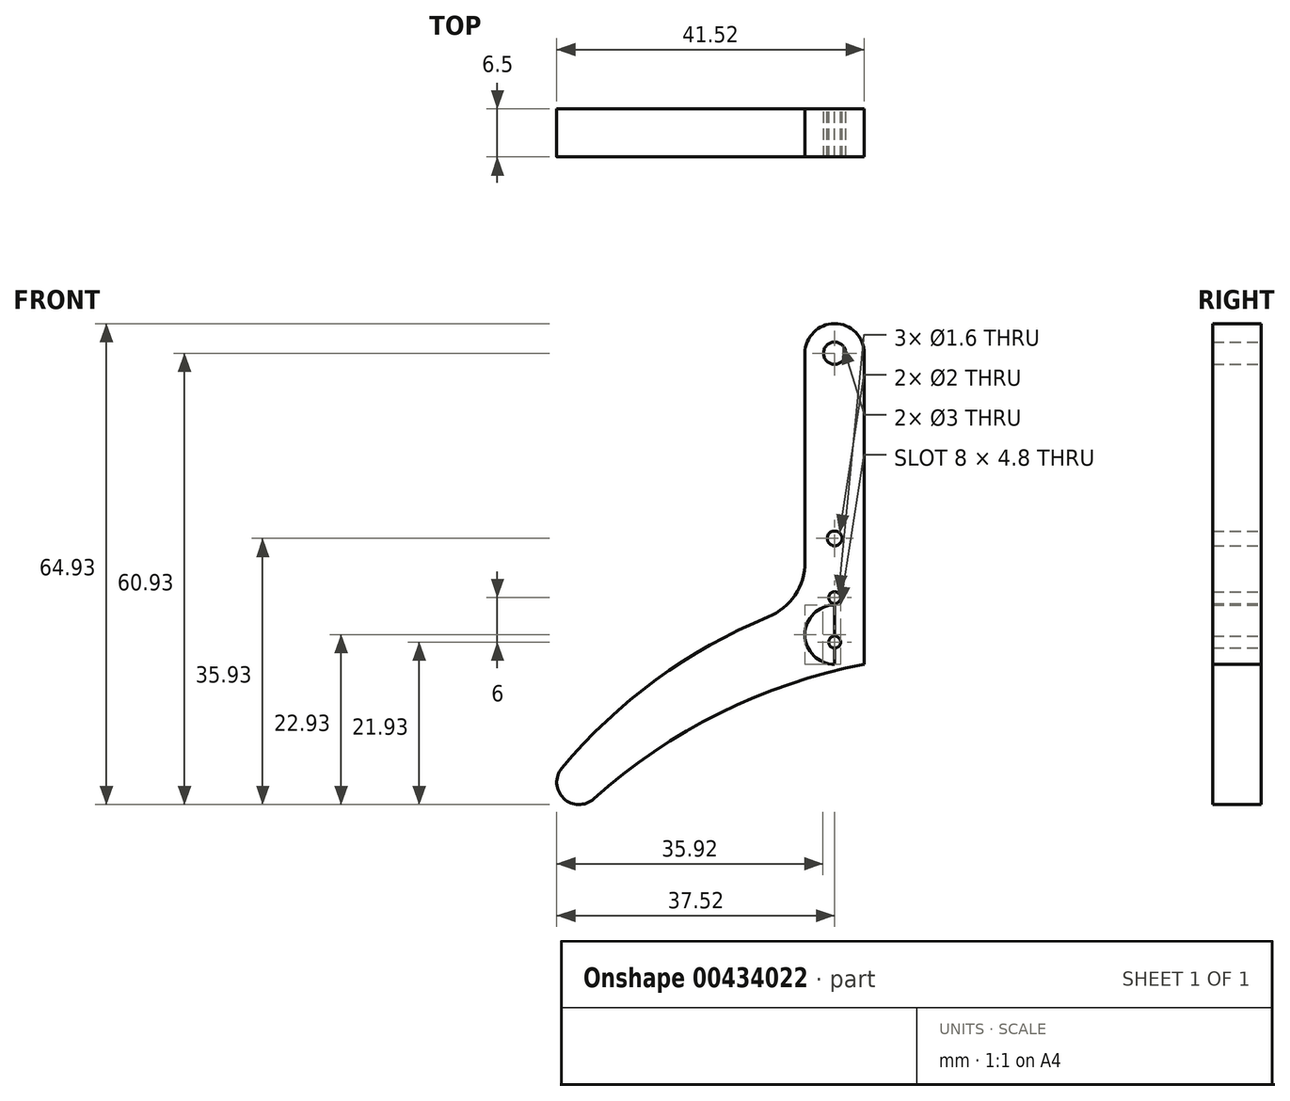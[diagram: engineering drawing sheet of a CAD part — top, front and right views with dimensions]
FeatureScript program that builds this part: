
annotation { "Feature Type Name" : "Feature", "Feature Type Description" : "" }
export const myFeature = defineFeature(function(context is Context, id is Id, definition is map)
    precondition{}
    {
        {
            var Q0;
            Q0=qCreatedBy(makeId("Front.planeOp"),FACE);
            var sketch = newSketch(context, id + "F0", { "sketchPlane" : qUnion([Q0])});
            skCircle(sketch, "E0", {"center": v(0, 38) * mm, "radius": 4 * mm});
            skCircle(sketch, "E1", {"center": v(0, 0) * mm, "radius": 4 * mm});
            skCircle(sketch, "E2", {"center": v(0, 38) * mm, "radius": 1.5 * mm});
            skCircle(sketch, "E3", {"center": v(-34.52, -19.93) * mm, "radius": 3 * mm});
            skLineSegment(sketch, "E4", {"start": v(-4, 38) * mm, "end": v(-4, 9.8) * mm});
            skLineSegment(sketch, "E5", {"start": v(4, 38) * mm, "end": v(4, 0) * mm});
            skCircle(sketch, "E6", {"center": v(0, 13) * mm, "radius": 1 * mm});
            skLineSegment(sketch, "E7.bottom", {"start": v(4, 0) * mm, "end": v(0, 0) * mm});
            skLineSegment(sketch, "E7.top", {"start": v(4, -4) * mm, "end": v(0, -4) * mm});
            skLineSegment(sketch, "E7.left", {"start": v(4, 0) * mm, "end": v(4, -4) * mm});
            skLineSegment(sketch, "E7.right", {"start": v(0, 0) * mm, "end": v(0, -4) * mm});
            skLineSegment(sketch, "E8.left", {"start": v(0, 0) * mm, "end": v(0, 31.99) * mm});
            skLineSegment(sketch, "E9", {"start": v(0, 0) * mm, "end": v(-34.52, -19.93) * mm, "construction": true});
            skPoint(sketch, "E10.visualSharp", {"position": v(-4, 0) * mm});
            skArc(sketch, "E11", {"start": v(4, -4) * mm, "mid": v(-15.5, -10.58) * mm, "end": v(-32.5, -22.16) * mm});
            skPoint(sketch, "E12", {"position": v(-4, 4.07) * mm});
            skArc(sketch, "E13", {"start": v(-8.95, 2.41) * mm, "mid": v(-24.12, -6.1) * mm, "end": v(-36.82, -18) * mm});
            skArc(sketch, "E14.filletArc", {"start": v(-8.95, 2.41) * mm, "mid": v(-5.35, 5.36) * mm, "end": v(-4, 9.8) * mm});
            skCircle(sketch, "E15", {"center": v(0, 5) * mm, "radius": 0.8 * mm});
            skCircle(sketch, "E16", {"center": v(0, -1) * mm, "radius": 0.8 * mm});
            skSolve(sketch);
        }
        {
            var Q0;
            Q0 = qSketchRegion(id + "F0", true);
            var Q1;
            {var subQ1=sQuery(id+"F0.wireOp",EDGE,"E1");var subQ3=sQuery(id+"F0.wireOp",EDGE,"E8.left");var subQ4=makeQuery(id+"F0.imprint","INTERSECT",VERTEX,{"derivedFrom":[subQ1,subQ3]});Q1=makeQuery(id+"F0.imprint","IMPRINT",FACE,{"disambiguationData":[TD([[makeQuery(id+"F0.imprint","IMPRINT",EDGE,{"disambiguationData":[TD([[subQ4,1.0]])],"derivedFrom":subQ3}),1.0]])]});}
            extrude(context, id + "F1", {"entities" : qUnion([Q0, Q1]), "depth" : 6.5 * mm});
        }
        {
            var Q0;
            Q0=makeQuery(id+"F0.imprint","IMPRINT",FACE,{"disambiguationData":[TD([[makeQuery(id+"F0.imprint","IMPRINT",EDGE,{"derivedFrom":sQuery(id+"F0.wireOp",EDGE,"E2")}),-1.0]])]});
            var Q1;
            {var subQ6=sQuery(id+"F0.wireOp",EDGE,"E4");Q1=makeQuery(id+"F0.imprint","IMPRINT",FACE,{"disambiguationData":[TD([[makeQuery(id+"F0.imprint","IMPRINT",EDGE,{"derivedFrom":subQ6}),1.0]])]});}
            var Q2;
            {var subQ1=sQuery(id+"F0.wireOp",EDGE,"E7.bottom");Q2=makeQuery(id+"F0.imprint","IMPRINT",FACE,{"disambiguationData":[TD([[makeQuery(id+"F0.imprint","IMPRINT",EDGE,{"derivedFrom":subQ1}),1.0]])]});}
            var Q3;
            {var subQ2=sQuery(id+"F0.wireOp",EDGE,"E7.top");Q3=makeQuery(id+"F0.imprint","IMPRINT",FACE,{"disambiguationData":[TD([[makeQuery(id+"F0.imprint","IMPRINT",EDGE,{"derivedFrom":subQ2}),-1.0]])]});}
            var Q4;
            {var subQ0=sQuery(id+"F0.wireOp",EDGE,"E7.right");var subQ3=sQuery(id+"F0.wireOp",EDGE,"E16");var subQ7=makeQuery(id+"F0.imprint","INTERSECT",VERTEX,{"disambiguationData":[OD(0.0)],"derivedFrom":[subQ0,subQ3]});Q4=makeQuery(id+"F0.imprint","IMPRINT",FACE,{"disambiguationData":[TD([[makeQuery(id+"F0.imprint","IMPRINT",EDGE,{"disambiguationData":[TD([[subQ7,-1.0]])],"derivedFrom":subQ3}),-1.0]])]});}
            var Q5;
            {var subQ0=sQuery(id+"F0.wireOp",EDGE,"E7.bottom");Q5=makeQuery(id+"F0.imprint","IMPRINT",FACE,{"disambiguationData":[TD([[makeQuery(id+"F0.imprint","IMPRINT",EDGE,{"derivedFrom":subQ0}),-1.0]])]});}
            var Q6;
            {var subQ0=sQuery(id+"F0.wireOp",EDGE,"E3");var subQ1=makeQuery(id+"F0.imprint","INTERSECT",VERTEX,{"derivedFrom":[subQ0,sQuery(id+"F0.wireOp",EDGE,"E11")]});Q6=makeQuery(id+"F0.imprint","IMPRINT",FACE,{"disambiguationData":[TD([[makeQuery(id+"F0.imprint","IMPRINT",EDGE,{"disambiguationData":[TD([[subQ1,1.0]])],"derivedFrom":subQ0}),1.0]])]});}
            extrude(context, id + "F2", {"entities" : qUnion([Q0, Q1, Q2, Q3, Q4, Q5, Q6]), "depth" : 6.5 * mm});
        }
    });
